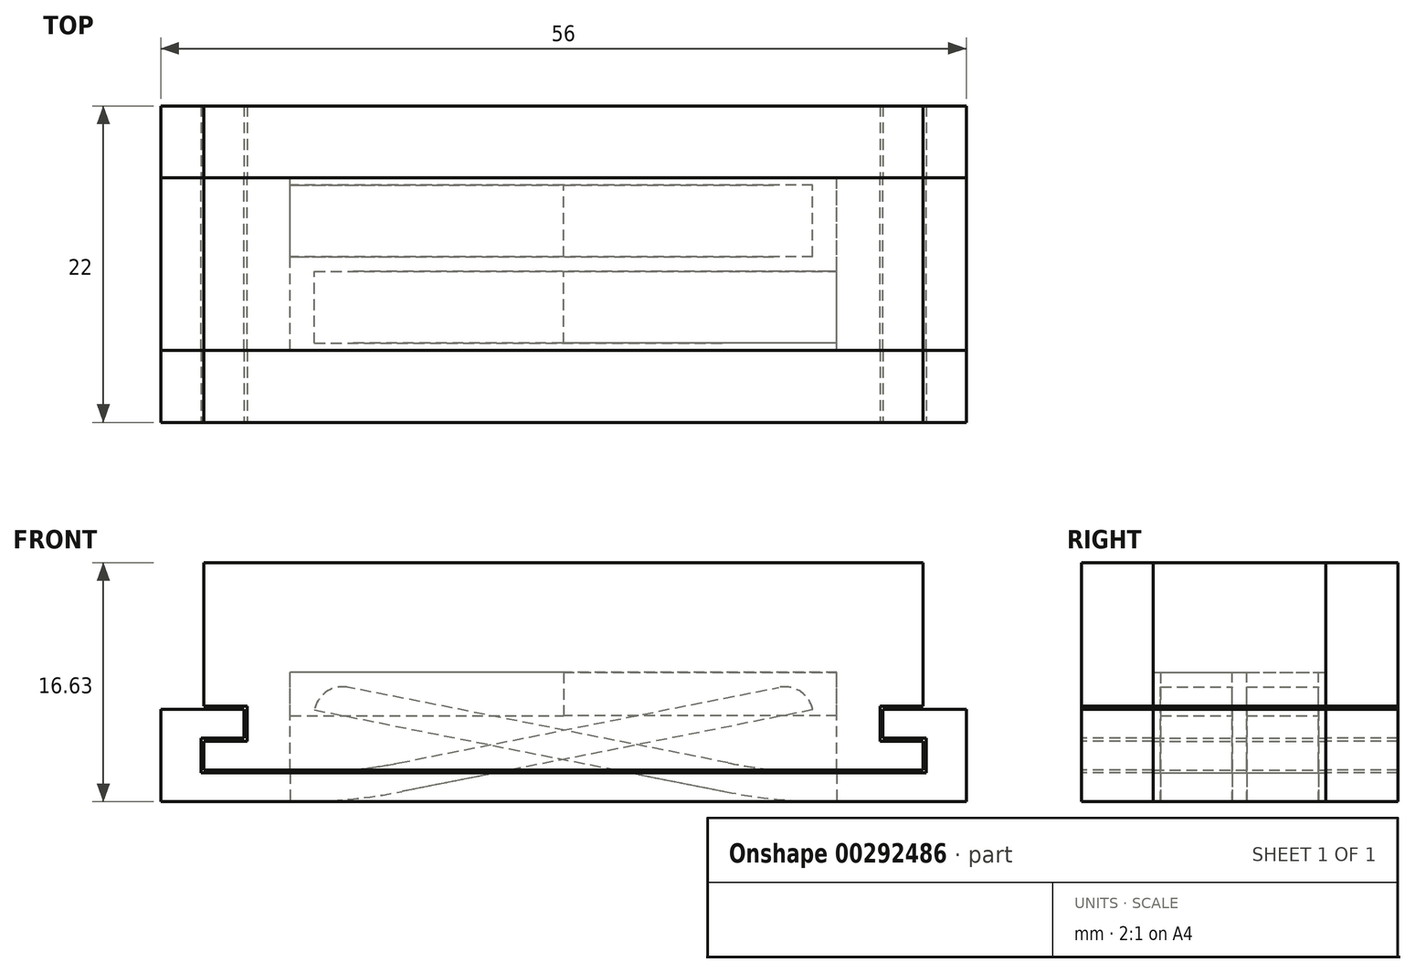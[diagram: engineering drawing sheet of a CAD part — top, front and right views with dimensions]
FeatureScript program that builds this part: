
annotation { "Feature Type Name" : "Feature", "Feature Type Description" : "" }
export const myFeature = defineFeature(function(context is Context, id is Id, definition is map)
    precondition{}
    {
        {
            var Q0;
            Q0=qCreatedBy(makeId("Front.planeOp"),FACE);
            var sketch = newSketch(context, id + "F0", { "sketchPlane" : qUnion([Q0])});
            skLineSegment(sketch, "E0.left", {"start": v(-25, 14.42) * mm, "end": v(-25, 4.42) * mm});
            skLineSegment(sketch, "E1.bottom", {"start": v(-28, 4.21) * mm, "end": v(-22.21, 4.21) * mm});
            skLineSegment(sketch, "E1.left", {"start": v(-28, 4.21) * mm, "end": v(-28, -2.21) * mm});
            skLineSegment(sketch, "E2", {"start": v(-22.21, 4.21) * mm, "end": v(-22.21, 2.21) * mm});
            skLineSegment(sketch, "E3", {"start": v(-22.21, 2.21) * mm, "end": v(-25.21, 2.21) * mm});
            skLineSegment(sketch, "E4", {"start": v(-25.21, 2.21) * mm, "end": v(-25.21, -0.21) * mm});
            skLineSegment(sketch, "E5", {"start": v(0, 21.12) * mm, "end": v(0, -6.27) * mm, "construction": true});
            skLineSegment(sketch, "E6", {"start": v(-25, 4.42) * mm, "end": v(-22, 4.42) * mm});
            skLineSegment(sketch, "E7", {"start": v(-22, 4.42) * mm, "end": v(-22, 2) * mm});
            skLineSegment(sketch, "E8", {"start": v(-22, 2) * mm, "end": v(-25, 2) * mm});
            skLineSegment(sketch, "E9", {"start": v(-22.21, 4.21) * mm, "end": v(-22, 4.42) * mm, "construction": true});
            skLineSegment(sketch, "E10", {"start": v(-22.21, 2.21) * mm, "end": v(-22, 2) * mm, "construction": true});
            skLineSegment(sketch, "E11", {"start": v(-25, 2) * mm, "end": v(-25.21, 2.21) * mm, "construction": true});
            skLineSegment(sketch, "E12", {"start": v(-25, 0) * mm, "end": v(-25.21, -0.21) * mm, "construction": true});
            skLineSegment(sketch, "E13", {"start": v(0, 0) * mm, "end": v(0.21, 0.21) * mm, "construction": true});
            skLineSegment(sketch, "E14.trimOffspring", {"start": v(-25, 2) * mm, "end": v(-25, 0) * mm});
            skLineSegment(sketch, "E15.MirrorCS", {"start": v(25, 0) * mm, "end": v(25.21, -0.21) * mm, "construction": true});
            skLineSegment(sketch, "E16.MirrorCS", {"start": v(22.21, 4.21) * mm, "end": v(22, 4.42) * mm, "construction": true});
            skLineSegment(sketch, "E17.MirrorCS", {"start": v(22.21, 2.21) * mm, "end": v(22, 2) * mm, "construction": true});
            skLineSegment(sketch, "E18.MirrorCS", {"start": v(25, 2) * mm, "end": v(25.21, 2.21) * mm, "construction": true});
            skLineSegment(sketch, "E19.MirrorCS", {"start": v(22, 4.42) * mm, "end": v(22, 2) * mm});
            skLineSegment(sketch, "E20.MirrorCS", {"start": v(25, 4.42) * mm, "end": v(22, 4.42) * mm});
            skLineSegment(sketch, "E21.MirrorCS", {"start": v(28, 4.21) * mm, "end": v(28, -2.21) * mm});
            skLineSegment(sketch, "E22.MirrorCS", {"start": v(22.21, 2.21) * mm, "end": v(25.21, 2.21) * mm});
            skLineSegment(sketch, "E23.MirrorCS", {"start": v(22.21, 4.21) * mm, "end": v(22.21, 2.21) * mm});
            skLineSegment(sketch, "E24.MirrorCS", {"start": v(25, 2) * mm, "end": v(25, 0) * mm});
            skLineSegment(sketch, "E25.MirrorCS", {"start": v(22, 2) * mm, "end": v(25, 2) * mm});
            skLineSegment(sketch, "E26.MirrorCS", {"start": v(28, 4.21) * mm, "end": v(22.21, 4.21) * mm});
            skLineSegment(sketch, "E27.MirrorCS", {"start": v(25, 14.42) * mm, "end": v(25, 4.42) * mm});
            skLineSegment(sketch, "E28.MirrorCS", {"start": v(25.21, 2.21) * mm, "end": v(25.21, -0.21) * mm});
            skLineSegment(sketch, "E29", {"start": v(-25, 14.42) * mm, "end": v(25, 14.42) * mm});
            skLineSegment(sketch, "E30", {"start": v(-28, -2.21) * mm, "end": v(28, -2.21) * mm});
            skLineSegment(sketch, "E31", {"start": v(-25.21, -0.21) * mm, "end": v(25.21, -0.21) * mm});
            skLineSegment(sketch, "E32", {"start": v(-25, 0) * mm, "end": v(25, 0) * mm});
            skSolve(sketch);
        }
        {
            var Q0;
            Q0=makeQuery(id+"F0.imprint","IMPRINT",FACE,{"disambiguationData":[TD([[makeQuery(id+"F0.imprint","IMPRINT",EDGE,{"derivedFrom":sQuery(id+"F0.wireOp",EDGE,"E1.bottom")}),-1.0]])]});
            var sketch = newSketch(context, id + "F1", { "sketchPlane" : qUnion([Q0])});
            skLineSegment(sketch, "E33", {"start": v(-11.43, 0.5) * mm, "end": v(14.97, 5.75) * mm});
            skArc(sketch, "E34", {"start": v(15.56, -0.21) * mm, "mid": v(15.41, 2.78) * mm, "end": v(14.97, 5.75) * mm, "construction": true});
            skLineSegment(sketch, "E35", {"start": v(17.32, 4.18) * mm, "end": v(-11.23, -1.5) * mm});
            skArc(sketch, "E36", {"start": v(18, -2.21) * mm, "mid": v(17.83, 1) * mm, "end": v(17.32, 4.18) * mm, "construction": true});
            skArc(sketch, "E37", {"start": v(17.32, 4.18) * mm, "mid": v(16.47, 5.45) * mm, "end": v(14.97, 5.75) * mm});
            skLineSegment(sketch, "E38", {"start": v(0, 5.79) * mm, "end": v(19, 5.79) * mm, "construction": true});
            skArc(sketch, "E39", {"start": v(-18.64, -0.21) * mm, "mid": v(-15.02, -0.03) * mm, "end": v(-11.43, 0.5) * mm});
            skArc(sketch, "E40", {"start": v(-18.45, -2.21) * mm, "mid": v(-14.82, -2.03) * mm, "end": v(-11.23, -1.5) * mm});
            skLineSegment(sketch, "E41.0", {"start": v(-28, -2.21) * mm, "end": v(-18.45, -2.21) * mm});
            skLineSegment(sketch, "E42.0", {"start": v(-28, 4.21) * mm, "end": v(-28, -2.21) * mm});
            skLineSegment(sketch, "E43.0", {"start": v(-28, 4.21) * mm, "end": v(-22.21, 4.21) * mm});
            skLineSegment(sketch, "E44.0", {"start": v(-22.21, 4.21) * mm, "end": v(-22.21, 2.21) * mm});
            skLineSegment(sketch, "E45.0", {"start": v(-22.21, 2.21) * mm, "end": v(-25.21, 2.21) * mm});
            skLineSegment(sketch, "E46.0", {"start": v(-25.21, 2.21) * mm, "end": v(-25.21, -0.21) * mm});
            skLineSegment(sketch, "E47.0", {"start": v(-25.21, -0.21) * mm, "end": v(-18.64, -0.21) * mm});
            skLineSegment(sketch, "E48.0", {"start": v(28, 4.21) * mm, "end": v(28, -2.21) * mm});
            skLineSegment(sketch, "E49.0", {"start": v(28, 4.21) * mm, "end": v(22.21, 4.21) * mm});
            skLineSegment(sketch, "E50.0", {"start": v(22.21, 4.21) * mm, "end": v(22.21, 2.21) * mm});
            skLineSegment(sketch, "E51.0", {"start": v(22.21, 2.21) * mm, "end": v(25.21, 2.21) * mm});
            skLineSegment(sketch, "E52.0", {"start": v(25.21, 2.21) * mm, "end": v(25.21, -0.21) * mm});
            skLineSegment(sketch, "E53.trimOffspring", {"start": v(19, -0.21) * mm, "end": v(25.21, -0.21) * mm});
            skLineSegment(sketch, "E54.trimOffspring", {"start": v(19, -2.21) * mm, "end": v(28, -2.21) * mm});
            skLineSegment(sketch, "E55", {"start": v(19, -0.21) * mm, "end": v(19, -2.21) * mm});
            skLineSegment(sketch, "E56.0", {"start": v(-25, 2) * mm, "end": v(-25, 0) * mm});
            skLineSegment(sketch, "E57.0", {"start": v(-22, 2) * mm, "end": v(-25, 2) * mm});
            skLineSegment(sketch, "E58.0", {"start": v(-22, 4.42) * mm, "end": v(-22, 2) * mm});
            skLineSegment(sketch, "E59.0", {"start": v(-25, 4.42) * mm, "end": v(-22, 4.42) * mm});
            skLineSegment(sketch, "E60.0", {"start": v(-25, 14.42) * mm, "end": v(-25, 4.42) * mm});
            skLineSegment(sketch, "E61.0", {"start": v(-25, 14.42) * mm, "end": v(25, 14.42) * mm});
            skLineSegment(sketch, "E62.0", {"start": v(25, 14.42) * mm, "end": v(25, 4.42) * mm});
            skLineSegment(sketch, "E63.0", {"start": v(25, 4.42) * mm, "end": v(22, 4.42) * mm});
            skLineSegment(sketch, "E64.0", {"start": v(22, 4.42) * mm, "end": v(22, 2) * mm});
            skLineSegment(sketch, "E65.0", {"start": v(22, 2) * mm, "end": v(25, 2) * mm});
            skLineSegment(sketch, "E66.0", {"start": v(25, 2) * mm, "end": v(25, 0) * mm});
            skLineSegment(sketch, "E67", {"start": v(-19, 0) * mm, "end": v(-19, 3.79) * mm});
            skLineSegment(sketch, "E68", {"start": v(19, 0) * mm, "end": v(19, 6.79) * mm});
            skLineSegment(sketch, "E69", {"start": v(19, 6.79) * mm, "end": v(0, 6.79) * mm});
            skLineSegment(sketch, "E70", {"start": v(-19, 3.79) * mm, "end": v(0, 3.79) * mm});
            skLineSegment(sketch, "E71", {"start": v(0, 6.79) * mm, "end": v(0, 3.79) * mm});
            skLineSegment(sketch, "E72.trimOffspring", {"start": v(19, 0) * mm, "end": v(25, 0) * mm});
            skLineSegment(sketch, "E73", {"start": v(-25, 0) * mm, "end": v(-19, 0) * mm});
            skLineSegment(sketch, "E74", {"start": v(-19, -0.21) * mm, "end": v(-19, -2.21) * mm});
            skLineSegment(sketch, "E75", {"start": v(0, 6.79) * mm, "end": v(-19, 6.79) * mm});
            skLineSegment(sketch, "E76", {"start": v(-19, 6.79) * mm, "end": v(-19, 3.79) * mm});
            skSolve(sketch);
        }
        {
            var Q0;
            Q0=makeQuery(id+"F1.imprint","IMPRINT",FACE,{"disambiguationData":[TD([[makeQuery(id+"F1.imprint","IMPRINT",EDGE,{"derivedFrom":sQuery(id+"F1.wireOp",EDGE,"E56.0")}),1.0]])]});
            var Q1;
            {var subQ0=sQuery(id+"F1.wireOp",EDGE,"E42.0");Q1=makeQuery(id+"F1.imprint","IMPRINT",FACE,{"disambiguationData":[TD([[makeQuery(id+"F1.imprint","IMPRINT",EDGE,{"derivedFrom":subQ0}),1.0]])]});}
            var Q2;
            Q2=makeQuery(id+"F1.imprint","IMPRINT",FACE,{"disambiguationData":[TD([[makeQuery(id+"F1.imprint","IMPRINT",EDGE,{"derivedFrom":sQuery(id+"F1.wireOp",EDGE,"E48.0")}),-1.0]])]});
            extrude(context, id + "F2", {"entities" : qUnion([Q0, Q1, Q2]), "depth" : 0.5 * mm});
        }
        {
            var Q0;
            Q0=makeQuery(id+"F1.imprint","IMPRINT",FACE,{"disambiguationData":[TD([[makeQuery(id+"F1.imprint","IMPRINT",EDGE,{"derivedFrom":sQuery(id+"F1.wireOp",EDGE,"E56.0")}),1.0]])]});
            var Q1;
            {var subQ0=sQuery(id+"F1.wireOp",EDGE,"E40");Q1=makeQuery(id+"F1.imprint","IMPRINT",FACE,{"disambiguationData":[TD([[makeQuery(id+"F1.imprint","IMPRINT",EDGE,{"derivedFrom":subQ0}),1.0]])]});}
            var Q2;
            Q2=makeQuery(id+"F1.imprint","IMPRINT",FACE,{"disambiguationData":[TD([[makeQuery(id+"F1.imprint","IMPRINT",EDGE,{"derivedFrom":sQuery(id+"F1.wireOp",EDGE,"E33")}),-1.0]])]});
            var Q3;
            Q3=makeQuery(id+"F1.imprint","IMPRINT",FACE,{"disambiguationData":[TD([[makeQuery(id+"F1.imprint","IMPRINT",EDGE,{"derivedFrom":sQuery(id+"F1.wireOp",EDGE,"E48.0")}),-1.0]])]});
            var Q4;
            {var subQ0=sQuery(id+"F1.wireOp",EDGE,"E42.0");Q4=makeQuery(id+"F1.imprint","IMPRINT",FACE,{"disambiguationData":[TD([[makeQuery(id+"F1.imprint","IMPRINT",EDGE,{"derivedFrom":subQ0}),1.0]])]});}
            var Q5;
            Q5=makeQuery(id+"F1.imprint","IMPRINT",FACE,{"disambiguationData":[TD([[makeQuery(id+"F1.imprint","IMPRINT",EDGE,{"derivedFrom":sQuery(id+"F1.wireOp",EDGE,"E70")}),1.0]])]});
            var Q6;
            Q6=makeQuery(id+"F2.opExtrude","CAP_FACE",FACE,{"disambiguationData":[OSD([sQuery(id+"F1.wireOp",EDGE,"E56.0"),sQuery(id+"F1.wireOp",EDGE,"E57.0"),sQuery(id+"F1.wireOp",EDGE,"E58.0"),sQuery(id+"F1.wireOp",EDGE,"E59.0"),sQuery(id+"F1.wireOp",EDGE,"E60.0"),sQuery(id+"F1.wireOp",EDGE,"E61.0"),sQuery(id+"F1.wireOp",EDGE,"E62.0"),sQuery(id+"F1.wireOp",EDGE,"E63.0"),sQuery(id+"F1.wireOp",EDGE,"E64.0"),sQuery(id+"F1.wireOp",EDGE,"E65.0"),sQuery(id+"F1.wireOp",EDGE,"E66.0"),sQuery(id+"F1.wireOp",EDGE,"E67"),sQuery(id+"F1.wireOp",EDGE,"E68"),sQuery(id+"F1.wireOp",EDGE,"E69"),sQuery(id+"F1.wireOp",EDGE,"E72.trimOffspring"),sQuery(id+"F1.wireOp",EDGE,"E73"),sQuery(id+"F1.wireOp",EDGE,"E75"),sQuery(id+"F1.wireOp",EDGE,"E76")])],"isStart":false});
            extrude(context, id + "F3", {"entities" : qUnion([Q0, Q1, Q2, Q3, Q4, Q5]), "operationType" : NewBodyOperationType.ADD, "depth" : 5.5 * mm, "hasSecondDirection" : true, "secondDirectionBound" : SecondDirectionBoundingType.UP_TO_SURFACE, "secondDirectionOppositeDirection" : false, "secondDirectionBoundEntityFace" : qUnion([Q6]), "secondDirectionDepth" : 25 * mm});
        }
        {
            var Q0;
            Q0=makeQuery(id+"F1.imprint","IMPRINT",FACE,{"disambiguationData":[TD([[makeQuery(id+"F1.imprint","IMPRINT",EDGE,{"derivedFrom":sQuery(id+"F1.wireOp",EDGE,"E48.0")}),-1.0]])]});
            var Q1;
            {var subQ0=sQuery(id+"F1.wireOp",EDGE,"E42.0");Q1=makeQuery(id+"F1.imprint","IMPRINT",FACE,{"disambiguationData":[TD([[makeQuery(id+"F1.imprint","IMPRINT",EDGE,{"derivedFrom":subQ0}),1.0]])]});}
            var Q2;
            Q2=makeQuery(id+"F1.imprint","IMPRINT",FACE,{"disambiguationData":[TD([[makeQuery(id+"F1.imprint","IMPRINT",EDGE,{"derivedFrom":sQuery(id+"F1.wireOp",EDGE,"E56.0")}),1.0]])]});
            var Q3;
            Q3=makeQuery(id+"F3.opExtrude","CAP_FACE",FACE,{"disambiguationData":[OSD([sQuery(id+"F1.wireOp",EDGE,"E56.0"),sQuery(id+"F1.wireOp",EDGE,"E57.0"),sQuery(id+"F1.wireOp",EDGE,"E58.0"),sQuery(id+"F1.wireOp",EDGE,"E59.0"),sQuery(id+"F1.wireOp",EDGE,"E60.0"),sQuery(id+"F1.wireOp",EDGE,"E61.0"),sQuery(id+"F1.wireOp",EDGE,"E62.0"),sQuery(id+"F1.wireOp",EDGE,"E63.0"),sQuery(id+"F1.wireOp",EDGE,"E64.0"),sQuery(id+"F1.wireOp",EDGE,"E65.0"),sQuery(id+"F1.wireOp",EDGE,"E66.0"),sQuery(id+"F1.wireOp",EDGE,"E67"),sQuery(id+"F1.wireOp",EDGE,"E68"),sQuery(id+"F1.wireOp",EDGE,"E69"),sQuery(id+"F1.wireOp",EDGE,"E72.trimOffspring"),sQuery(id+"F1.wireOp",EDGE,"E73"),sQuery(id+"F1.wireOp",EDGE,"E75"),sQuery(id+"F1.wireOp",EDGE,"E76")])],"isStart":false});
            extrude(context, id + "F4", {"entities" : qUnion([Q0, Q1, Q2]), "operationType" : NewBodyOperationType.ADD, "depth" : 6 * mm, "hasSecondDirection" : true, "secondDirectionBound" : SecondDirectionBoundingType.UP_TO_SURFACE, "secondDirectionOppositeDirection" : false, "secondDirectionBoundEntityFace" : qUnion([Q3]), "secondDirectionDepth" : 25 * mm});
        }
        {
            var Q0;
            Q0=makeQuery(id+"F2.opExtrude","SWEPT_BODY",BODY,{"disambiguationData":[OSD([sQuery(id+"F1.wireOp",EDGE,"E41.0"),sQuery(id+"F1.wireOp",EDGE,"E42.0"),sQuery(id+"F1.wireOp",EDGE,"E43.0"),sQuery(id+"F1.wireOp",EDGE,"E44.0"),sQuery(id+"F1.wireOp",EDGE,"E45.0"),sQuery(id+"F1.wireOp",EDGE,"E46.0"),sQuery(id+"F1.wireOp",EDGE,"E47.0"),sQuery(id+"F1.wireOp",EDGE,"E74")])]});
            var Q1;
            Q1=makeQuery(id+"F2.opExtrude","SWEPT_BODY",BODY,{"disambiguationData":[OSD([sQuery(id+"F1.wireOp",EDGE,"E56.0"),sQuery(id+"F1.wireOp",EDGE,"E57.0"),sQuery(id+"F1.wireOp",EDGE,"E58.0"),sQuery(id+"F1.wireOp",EDGE,"E59.0"),sQuery(id+"F1.wireOp",EDGE,"E60.0"),sQuery(id+"F1.wireOp",EDGE,"E61.0"),sQuery(id+"F1.wireOp",EDGE,"E62.0"),sQuery(id+"F1.wireOp",EDGE,"E63.0"),sQuery(id+"F1.wireOp",EDGE,"E64.0"),sQuery(id+"F1.wireOp",EDGE,"E65.0"),sQuery(id+"F1.wireOp",EDGE,"E66.0"),sQuery(id+"F1.wireOp",EDGE,"E67"),sQuery(id+"F1.wireOp",EDGE,"E68"),sQuery(id+"F1.wireOp",EDGE,"E69"),sQuery(id+"F1.wireOp",EDGE,"E72.trimOffspring"),sQuery(id+"F1.wireOp",EDGE,"E73"),sQuery(id+"F1.wireOp",EDGE,"E75"),sQuery(id+"F1.wireOp",EDGE,"E76")])]});
            var Q2;
            Q2=makeQuery(id+"F2.opExtrude","SWEPT_BODY",BODY,{"disambiguationData":[OSD([sQuery(id+"F1.wireOp",EDGE,"E48.0"),sQuery(id+"F1.wireOp",EDGE,"E49.0"),sQuery(id+"F1.wireOp",EDGE,"E50.0"),sQuery(id+"F1.wireOp",EDGE,"E51.0"),sQuery(id+"F1.wireOp",EDGE,"E52.0"),sQuery(id+"F1.wireOp",EDGE,"E53.trimOffspring"),sQuery(id+"F1.wireOp",EDGE,"E54.trimOffspring"),sQuery(id+"F1.wireOp",EDGE,"E55")])]});
            var Q3;
            Q3=qCreatedBy(makeId("Right.planeOp"),FACE);
            mirror(context, id + "F5", {"entities" : qUnion([Q0, Q1, Q2]), "mirrorPlane" : qUnion([Q3])});
        }
        {
            var Q0;
            Q0=makeQuery(id+"F5.opPattern","COPY",BODY,{"derivedFrom":makeQuery(id+"F2.opExtrude","SWEPT_BODY",BODY,{"disambiguationData":[OSD([sQuery(id+"F1.wireOp",EDGE,"E41.0"),sQuery(id+"F1.wireOp",EDGE,"E42.0"),sQuery(id+"F1.wireOp",EDGE,"E43.0"),sQuery(id+"F1.wireOp",EDGE,"E44.0"),sQuery(id+"F1.wireOp",EDGE,"E45.0"),sQuery(id+"F1.wireOp",EDGE,"E46.0"),sQuery(id+"F1.wireOp",EDGE,"E47.0"),sQuery(id+"F1.wireOp",EDGE,"E74")])]}),"instanceName":"1"});
            var Q1;
            Q1=makeQuery(id+"F5.opPattern","COPY",BODY,{"derivedFrom":makeQuery(id+"F2.opExtrude","SWEPT_BODY",BODY,{"disambiguationData":[OSD([sQuery(id+"F1.wireOp",EDGE,"E48.0"),sQuery(id+"F1.wireOp",EDGE,"E49.0"),sQuery(id+"F1.wireOp",EDGE,"E50.0"),sQuery(id+"F1.wireOp",EDGE,"E51.0"),sQuery(id+"F1.wireOp",EDGE,"E52.0"),sQuery(id+"F1.wireOp",EDGE,"E53.trimOffspring"),sQuery(id+"F1.wireOp",EDGE,"E54.trimOffspring"),sQuery(id+"F1.wireOp",EDGE,"E55")])]}),"instanceName":"1"});
            var Q2;
            Q2=makeQuery(id+"F5.opPattern","COPY",BODY,{"derivedFrom":makeQuery(id+"F2.opExtrude","SWEPT_BODY",BODY,{"disambiguationData":[OSD([sQuery(id+"F1.wireOp",EDGE,"E56.0"),sQuery(id+"F1.wireOp",EDGE,"E57.0"),sQuery(id+"F1.wireOp",EDGE,"E58.0"),sQuery(id+"F1.wireOp",EDGE,"E59.0"),sQuery(id+"F1.wireOp",EDGE,"E60.0"),sQuery(id+"F1.wireOp",EDGE,"E61.0"),sQuery(id+"F1.wireOp",EDGE,"E62.0"),sQuery(id+"F1.wireOp",EDGE,"E63.0"),sQuery(id+"F1.wireOp",EDGE,"E64.0"),sQuery(id+"F1.wireOp",EDGE,"E65.0"),sQuery(id+"F1.wireOp",EDGE,"E66.0"),sQuery(id+"F1.wireOp",EDGE,"E67"),sQuery(id+"F1.wireOp",EDGE,"E68"),sQuery(id+"F1.wireOp",EDGE,"E69"),sQuery(id+"F1.wireOp",EDGE,"E72.trimOffspring"),sQuery(id+"F1.wireOp",EDGE,"E73"),sQuery(id+"F1.wireOp",EDGE,"E75"),sQuery(id+"F1.wireOp",EDGE,"E76")])]}),"instanceName":"1"});
            var Q3;
            {var subQ0=sQuery(id+"F1.wireOp",EDGE,"E54.trimOffspring");var subQ1=sQuery(id+"F1.wireOp",EDGE,"E48.0");Q3=makeQuery(id+"F4.boolean.opBoolean","MERGE",EDGE,{"derivedFrom":[makeQuery(id+"F3.opExtrude","SWEPT_EDGE",EDGE,{"disambiguationData":[OSD([subQ1,subQ0])]}),makeQuery(id+"F4.opExtrude","SWEPT_EDGE",EDGE,{"disambiguationData":[OSD([subQ1,subQ0])]})]});}
            transform(context, id + "F6", {"entities" : qUnion([Q0, Q1, Q2]), "transformType" : TransformType.TRANSLATION_ENTITY, "oppositeDirectionEntity" : true, "transformLine" : qUnion([Q3]), "makeCopy" : false});
        }
        {
            var Q0;
            Q0=makeQuery(id+"F5.opPattern","COPY",BODY,{"derivedFrom":makeQuery(id+"F2.opExtrude","SWEPT_BODY",BODY,{"disambiguationData":[OSD([sQuery(id+"F1.wireOp",EDGE,"E56.0"),sQuery(id+"F1.wireOp",EDGE,"E57.0"),sQuery(id+"F1.wireOp",EDGE,"E58.0"),sQuery(id+"F1.wireOp",EDGE,"E59.0"),sQuery(id+"F1.wireOp",EDGE,"E60.0"),sQuery(id+"F1.wireOp",EDGE,"E61.0"),sQuery(id+"F1.wireOp",EDGE,"E62.0"),sQuery(id+"F1.wireOp",EDGE,"E63.0"),sQuery(id+"F1.wireOp",EDGE,"E64.0"),sQuery(id+"F1.wireOp",EDGE,"E65.0"),sQuery(id+"F1.wireOp",EDGE,"E66.0"),sQuery(id+"F1.wireOp",EDGE,"E67"),sQuery(id+"F1.wireOp",EDGE,"E68"),sQuery(id+"F1.wireOp",EDGE,"E69"),sQuery(id+"F1.wireOp",EDGE,"E72.trimOffspring"),sQuery(id+"F1.wireOp",EDGE,"E73"),sQuery(id+"F1.wireOp",EDGE,"E75"),sQuery(id+"F1.wireOp",EDGE,"E76")])]}),"instanceName":"1"});
            var Q1;
            Q1=makeQuery(id+"F2.opExtrude","SWEPT_BODY",BODY,{"disambiguationData":[OSD([sQuery(id+"F1.wireOp",EDGE,"E56.0"),sQuery(id+"F1.wireOp",EDGE,"E57.0"),sQuery(id+"F1.wireOp",EDGE,"E58.0"),sQuery(id+"F1.wireOp",EDGE,"E59.0"),sQuery(id+"F1.wireOp",EDGE,"E60.0"),sQuery(id+"F1.wireOp",EDGE,"E61.0"),sQuery(id+"F1.wireOp",EDGE,"E62.0"),sQuery(id+"F1.wireOp",EDGE,"E63.0"),sQuery(id+"F1.wireOp",EDGE,"E64.0"),sQuery(id+"F1.wireOp",EDGE,"E65.0"),sQuery(id+"F1.wireOp",EDGE,"E66.0"),sQuery(id+"F1.wireOp",EDGE,"E67"),sQuery(id+"F1.wireOp",EDGE,"E68"),sQuery(id+"F1.wireOp",EDGE,"E69"),sQuery(id+"F1.wireOp",EDGE,"E72.trimOffspring"),sQuery(id+"F1.wireOp",EDGE,"E73"),sQuery(id+"F1.wireOp",EDGE,"E75"),sQuery(id+"F1.wireOp",EDGE,"E76")])]});
            var Q2;
            Q2=makeQuery(id+"F2.opExtrude","SWEPT_BODY",BODY,{"disambiguationData":[OSD([sQuery(id+"F1.wireOp",EDGE,"E41.0"),sQuery(id+"F1.wireOp",EDGE,"E42.0"),sQuery(id+"F1.wireOp",EDGE,"E43.0"),sQuery(id+"F1.wireOp",EDGE,"E44.0"),sQuery(id+"F1.wireOp",EDGE,"E45.0"),sQuery(id+"F1.wireOp",EDGE,"E46.0"),sQuery(id+"F1.wireOp",EDGE,"E47.0"),sQuery(id+"F1.wireOp",EDGE,"E74")])]});
            var Q3;
            Q3=makeQuery(id+"F5.opPattern","COPY",BODY,{"derivedFrom":makeQuery(id+"F2.opExtrude","SWEPT_BODY",BODY,{"disambiguationData":[OSD([sQuery(id+"F1.wireOp",EDGE,"E48.0"),sQuery(id+"F1.wireOp",EDGE,"E49.0"),sQuery(id+"F1.wireOp",EDGE,"E50.0"),sQuery(id+"F1.wireOp",EDGE,"E51.0"),sQuery(id+"F1.wireOp",EDGE,"E52.0"),sQuery(id+"F1.wireOp",EDGE,"E53.trimOffspring"),sQuery(id+"F1.wireOp",EDGE,"E54.trimOffspring"),sQuery(id+"F1.wireOp",EDGE,"E55")])]}),"instanceName":"1"});
            var Q4;
            Q4=makeQuery(id+"F2.opExtrude","SWEPT_BODY",BODY,{"disambiguationData":[OSD([sQuery(id+"F1.wireOp",EDGE,"E48.0"),sQuery(id+"F1.wireOp",EDGE,"E49.0"),sQuery(id+"F1.wireOp",EDGE,"E50.0"),sQuery(id+"F1.wireOp",EDGE,"E51.0"),sQuery(id+"F1.wireOp",EDGE,"E52.0"),sQuery(id+"F1.wireOp",EDGE,"E53.trimOffspring"),sQuery(id+"F1.wireOp",EDGE,"E54.trimOffspring"),sQuery(id+"F1.wireOp",EDGE,"E55")])]});
            var Q5;
            Q5=makeQuery(id+"F5.opPattern","COPY",BODY,{"derivedFrom":makeQuery(id+"F2.opExtrude","SWEPT_BODY",BODY,{"disambiguationData":[OSD([sQuery(id+"F1.wireOp",EDGE,"E41.0"),sQuery(id+"F1.wireOp",EDGE,"E42.0"),sQuery(id+"F1.wireOp",EDGE,"E43.0"),sQuery(id+"F1.wireOp",EDGE,"E44.0"),sQuery(id+"F1.wireOp",EDGE,"E45.0"),sQuery(id+"F1.wireOp",EDGE,"E46.0"),sQuery(id+"F1.wireOp",EDGE,"E47.0"),sQuery(id+"F1.wireOp",EDGE,"E74")])]}),"instanceName":"1"});
            booleanBodies(context, id + "F7", {"operationType" : BooleanOperationType.UNION, "tools" : qUnion([Q0, Q1, Q2, Q3, Q4, Q5])});
        }
        {
            var Q0;
            Q0=makeQuery(id+"F0.imprint","IMPRINT",FACE,{"disambiguationData":[TD([[makeQuery(id+"F0.imprint","IMPRINT",EDGE,{"derivedFrom":sQuery(id+"F0.wireOp",EDGE,"E1.bottom")}),-1.0]])]});
            var Q1;
            Q1=makeQuery(id+"F0.imprint","IMPRINT",FACE,{"disambiguationData":[TD([[makeQuery(id+"F0.imprint","IMPRINT",EDGE,{"derivedFrom":sQuery(id+"F0.wireOp",EDGE,"E0.left")}),1.0]])]});
            extrude(context, id + "F8", {"entities" : qUnion([Q0, Q1]), "oppositeDirection" : true, "depth" : 5 * mm});
        }
        {
            var Q0;
            Q0=makeQuery(id+"F8.opExtrude","SWEPT_BODY",BODY,{"disambiguationData":[OSD([sQuery(id+"F0.wireOp",EDGE,"E1.bottom"),sQuery(id+"F0.wireOp",EDGE,"E1.left"),sQuery(id+"F0.wireOp",EDGE,"E2"),sQuery(id+"F0.wireOp",EDGE,"E3"),sQuery(id+"F0.wireOp",EDGE,"E4"),sQuery(id+"F0.wireOp",EDGE,"E21.MirrorCS"),sQuery(id+"F0.wireOp",EDGE,"E22.MirrorCS"),sQuery(id+"F0.wireOp",EDGE,"E23.MirrorCS"),sQuery(id+"F0.wireOp",EDGE,"E26.MirrorCS"),sQuery(id+"F0.wireOp",EDGE,"E28.MirrorCS"),sQuery(id+"F0.wireOp",EDGE,"E30"),sQuery(id+"F0.wireOp",EDGE,"E31")])]});
            var Q1;
            Q1=makeQuery(id+"F8.opExtrude","SWEPT_BODY",BODY,{"disambiguationData":[OSD([sQuery(id+"F0.wireOp",EDGE,"E0.left"),sQuery(id+"F0.wireOp",EDGE,"E6"),sQuery(id+"F0.wireOp",EDGE,"E7"),sQuery(id+"F0.wireOp",EDGE,"E8"),sQuery(id+"F0.wireOp",EDGE,"E14.trimOffspring"),sQuery(id+"F0.wireOp",EDGE,"E19.MirrorCS"),sQuery(id+"F0.wireOp",EDGE,"E20.MirrorCS"),sQuery(id+"F0.wireOp",EDGE,"E24.MirrorCS"),sQuery(id+"F0.wireOp",EDGE,"E25.MirrorCS"),sQuery(id+"F0.wireOp",EDGE,"E27.MirrorCS"),sQuery(id+"F0.wireOp",EDGE,"E29"),sQuery(id+"F0.wireOp",EDGE,"E32")])]});
            var Q2;
            {var subQ0=sQuery(id+"F1.wireOp",EDGE,"E42.0");var subQ1=sQuery(id+"F1.wireOp",EDGE,"E41.0");var subQ2=sQuery(id+"F1.wireOp",EDGE,"E54.trimOffspring");var subQ3=sQuery(id+"F1.wireOp",EDGE,"E48.0");Q2=makeQuery(id+"F7.opBoolean","MERGE",EDGE,{"derivedFrom":[makeQuery(id+"F4.boolean.opBoolean","MERGE",EDGE,{"derivedFrom":[makeQuery(id+"F3.boolean.opBoolean","MERGE",EDGE,{"derivedFrom":[makeQuery(id+"F2.opExtrude","SWEPT_EDGE",EDGE,{"disambiguationData":[OSD([subQ3,subQ2])]}),makeQuery(id+"F3.opExtrude","SWEPT_EDGE",EDGE,{"disambiguationData":[OSD([subQ3,subQ2])]})]}),makeQuery(id+"F4.opExtrude","SWEPT_EDGE",EDGE,{"disambiguationData":[OSD([subQ3,subQ2])]})]}),makeQuery(id+"F5.opPattern","COPY",EDGE,{"derivedFrom":makeQuery(id+"F4.boolean.opBoolean","MERGE",EDGE,{"derivedFrom":[makeQuery(id+"F3.boolean.opBoolean","MERGE",EDGE,{"derivedFrom":[makeQuery(id+"F2.opExtrude","SWEPT_EDGE",EDGE,{"disambiguationData":[OSD([subQ1,subQ0])]}),makeQuery(id+"F3.opExtrude","SWEPT_EDGE",EDGE,{"disambiguationData":[OSD([subQ1,subQ0])]})]}),makeQuery(id+"F4.opExtrude","SWEPT_EDGE",EDGE,{"disambiguationData":[OSD([subQ1,subQ0])]})]}),"instanceName":"1"})]});}
            transform(context, id + "F9", {"entities" : qUnion([Q0, Q1]), "transformType" : TransformType.TRANSLATION_DISTANCE, "transformDirection" : qUnion([Q2]), "distance" : (12 + 5) * mm, "oppositeDirection" : true, "makeCopy" : true});
        }
    });
